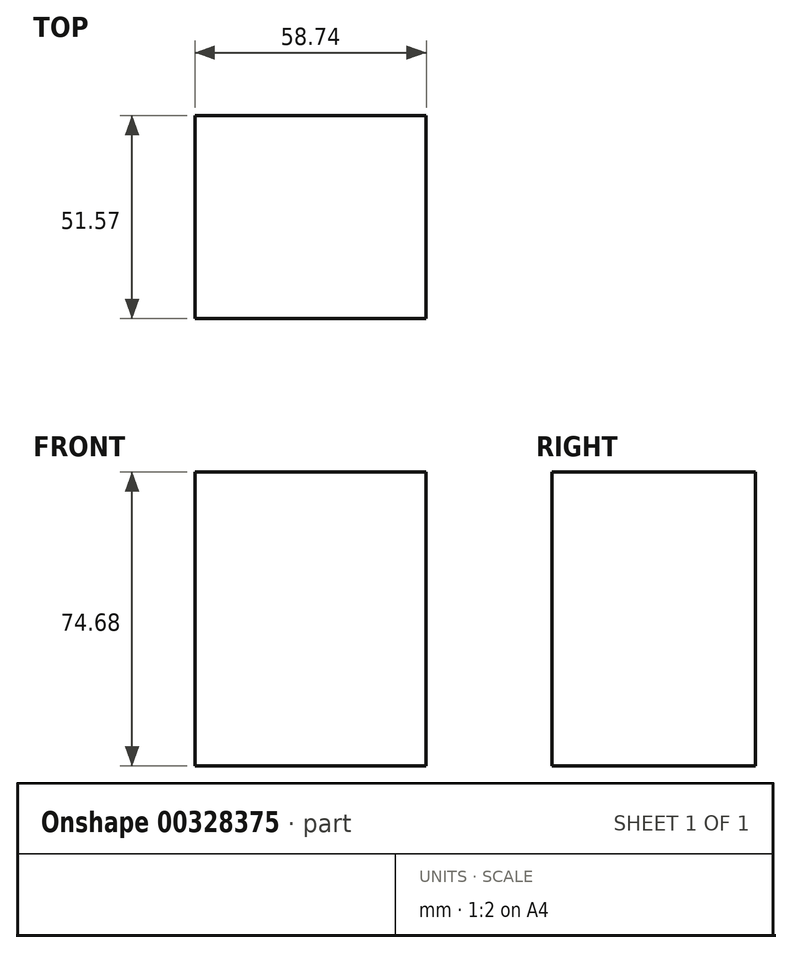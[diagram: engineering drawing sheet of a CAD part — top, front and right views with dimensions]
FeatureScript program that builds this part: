
annotation { "Feature Type Name" : "Feature", "Feature Type Description" : "" }
export const myFeature = defineFeature(function(context is Context, id is Id, definition is map)
    precondition{}
    {
        {
            var Q0;
            Q0=qCreatedBy(makeId("Top.planeOp"),FACE);
            var sketch = newSketch(context, id + "F0", { "sketchPlane" : qUnion([Q0])});
            skLineSegment(sketch, "E0.bottom", {"start": v(-31.45, 22.2) * mm, "end": v(27.29, 22.2) * mm});
            skLineSegment(sketch, "E0.top", {"start": v(-31.45, -29.37) * mm, "end": v(27.29, -29.37) * mm});
            skLineSegment(sketch, "E0.left", {"start": v(-31.45, 22.2) * mm, "end": v(-31.45, -29.37) * mm});
            skLineSegment(sketch, "E0.right", {"start": v(27.29, 22.2) * mm, "end": v(27.29, -29.37) * mm});
            skSolve(sketch);
        }
        {
            var Q0;
            Q0=makeQuery(id+"F0.imprint","IMPRINT",FACE,{"disambiguationData":[TD([[makeQuery(id+"F0.imprint","IMPRINT",EDGE,{"derivedFrom":sQuery(id+"F0.wireOp",EDGE,"E0.bottom")}),-1.0]])]});
            extrude(context, id + "F1", {"entities" : qUnion([Q0]), "oppositeDirection" : true, "depth" : 74.68 * mm});
        }
    });
